# Revit family: LED QUADRATE 01_AM18W.2.12
name_source: partatom
category: Luminarias
units: mm (PartAtom-declared; Revit-internal decimal feet)

## family parameters
Compartido = No
Corte con vacíos al cargar = No
Cota de conector redondo = Diámetro de uso
Origen de luz = Sí
Punto de cálculo de habitación = No
Se basa en plano de trabajo = Sí
Siempre vertical = No
Tipo de pieza = Normal

## types (1)
- LED QUADRATE 01_AM18W.2.12
    Archivo de red fotométrica = AM18W.2_12°.IES
    Cambio de temperatura de color de luz atenuada = <Ninguno>
    Comentarios de vataje = 100-277V
    Descripción = LUMINARIA DIRIGIBLE TIPO ARBOTANTE, DE MATERIAL EN ALUMINIO FUNDIDO A PRESION CUBIERTO CON POLVO GRIS OSCURO Y VIDRIO DE 3MM, CON UN PESO DE 2.5KG, CON 1 LED TIPO NICHIA Y UNA POTENCIA TOTAL DE 20W, 1705 LUMENES, TEMPERATURA EN BLANCO CALIDO 3000K, IRC 80, IP 65, APERTURA DE 12 GRADOS POR PROYECTO, CORRIENTE DE OPERACIÓN 178mA, CABLE DE 0.3M, ALIMENTADO A 100-277VAC
    Elevación por defecto = 0 mm  [stored 0 ft]
    Fabricante = BRILLANT
    Filtro de color = 16777215
    Lámpara = NICHIA
    Modelo = AM18W.2.12
    Watt per fixture = 20
    Ángulo de inclinación = 60.00°

note: [stored X ft] marks values corroborated as IEEE doubles in the binary element streams (Revit-internal decimal feet)

## geometry (parser evidence)
native form markers: Blend x2
no freeform markers — native parametric forms only
